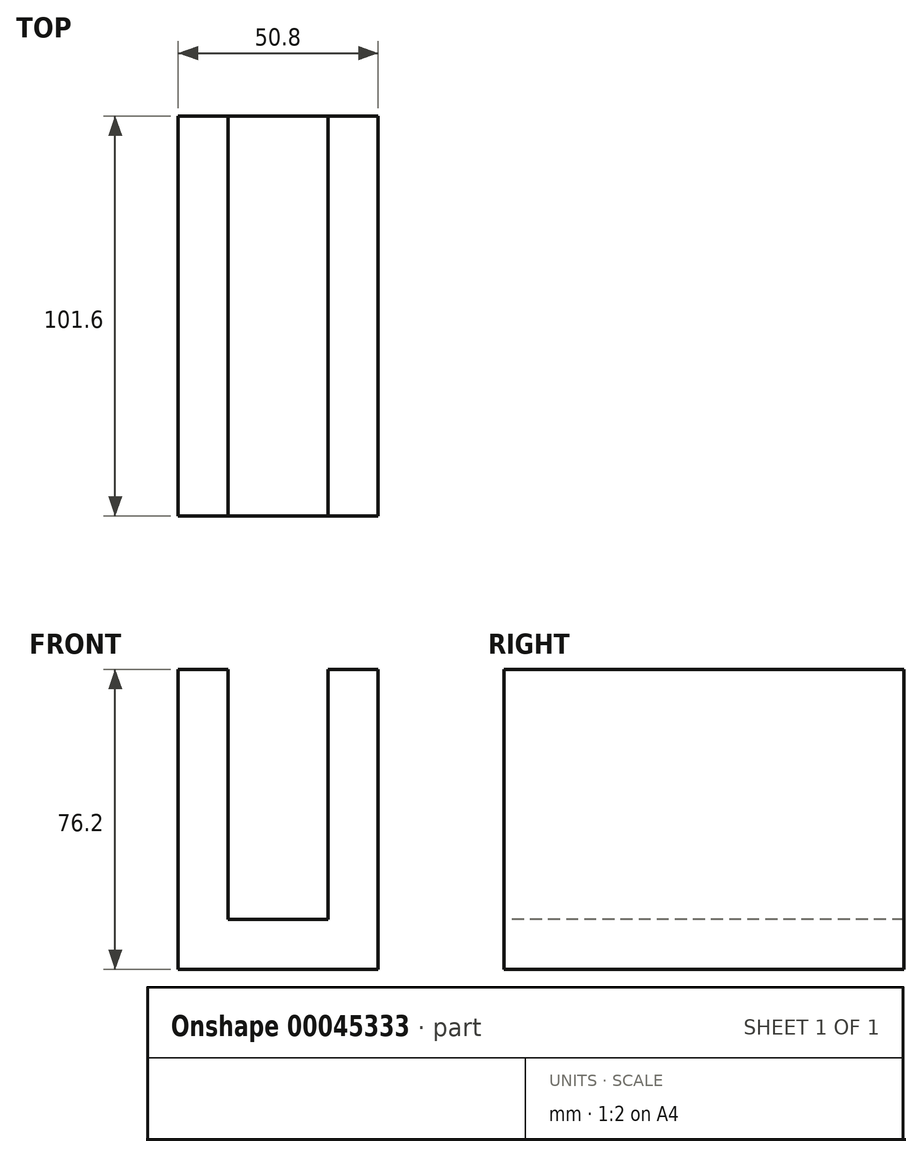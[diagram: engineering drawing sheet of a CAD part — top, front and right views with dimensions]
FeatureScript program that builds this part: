
annotation { "Feature Type Name" : "Feature", "Feature Type Description" : "" }
export const myFeature = defineFeature(function(context is Context, id is Id, definition is map)
    precondition{}
    {
        {
            var Q0;
            Q0=qCreatedBy(makeId("Front.planeOp"),FACE);
            var sketch = newSketch(context, id + "F0", { "sketchPlane" : qUnion([Q0])});
            skLineSegment(sketch, "E0.bottom", {"start": v(0, 0) * mm, "end": v(50.8, 0) * mm});
            skLineSegment(sketch, "E0.top", {"start": v(0, 76.2) * mm, "end": v(50.8, 76.2) * mm});
            skLineSegment(sketch, "E0.left", {"start": v(0, 0) * mm, "end": v(0, 76.2) * mm});
            skLineSegment(sketch, "E0.right", {"start": v(50.8, 0) * mm, "end": v(50.8, 76.2) * mm});
            skSolve(sketch);
        }
        {
            var Q0;
            Q0 = qSketchRegion(id + "F0", true);
            extrude(context, id + "F1", {"entities" : qUnion([Q0]), "depth" : 101.6 * mm});
        }
        {
            var Q0;
            Q0=makeQuery(id+"F1.opExtrude","CAP_FACE",FACE,{"disambiguationData":[OSD([sQuery(id+"F0.wireOp",EDGE,"E0.bottom"),sQuery(id+"F0.wireOp",EDGE,"E0.top"),sQuery(id+"F0.wireOp",EDGE,"E0.left"),sQuery(id+"F0.wireOp",EDGE,"E0.right")])],"isStart":false});
            var sketch = newSketch(context, id + "F2", { "sketchPlane" : qUnion([Q0])});
            skLineSegment(sketch, "E1.bottom", {"start": v(12.7, 76.2) * mm, "end": v(38.1, 76.2) * mm});
            skLineSegment(sketch, "E1.top", {"start": v(12.7, 12.7) * mm, "end": v(38.1, 12.7) * mm});
            skLineSegment(sketch, "E1.left", {"start": v(12.7, 76.2) * mm, "end": v(12.7, 12.7) * mm});
            skLineSegment(sketch, "E1.right", {"start": v(38.1, 76.2) * mm, "end": v(38.1, 12.7) * mm});
            skSolve(sketch);
        }
        {
            var Q0;
            Q0 = qSketchRegion(id + "F2", true);
            extrude(context, id + "F3", {"entities" : qUnion([Q0]), "operationType" : NewBodyOperationType.REMOVE, "endBound" : BoundingType.UP_TO_NEXT, "oppositeDirection" : true, "depth" : 25.4 * mm});
        }
    });
